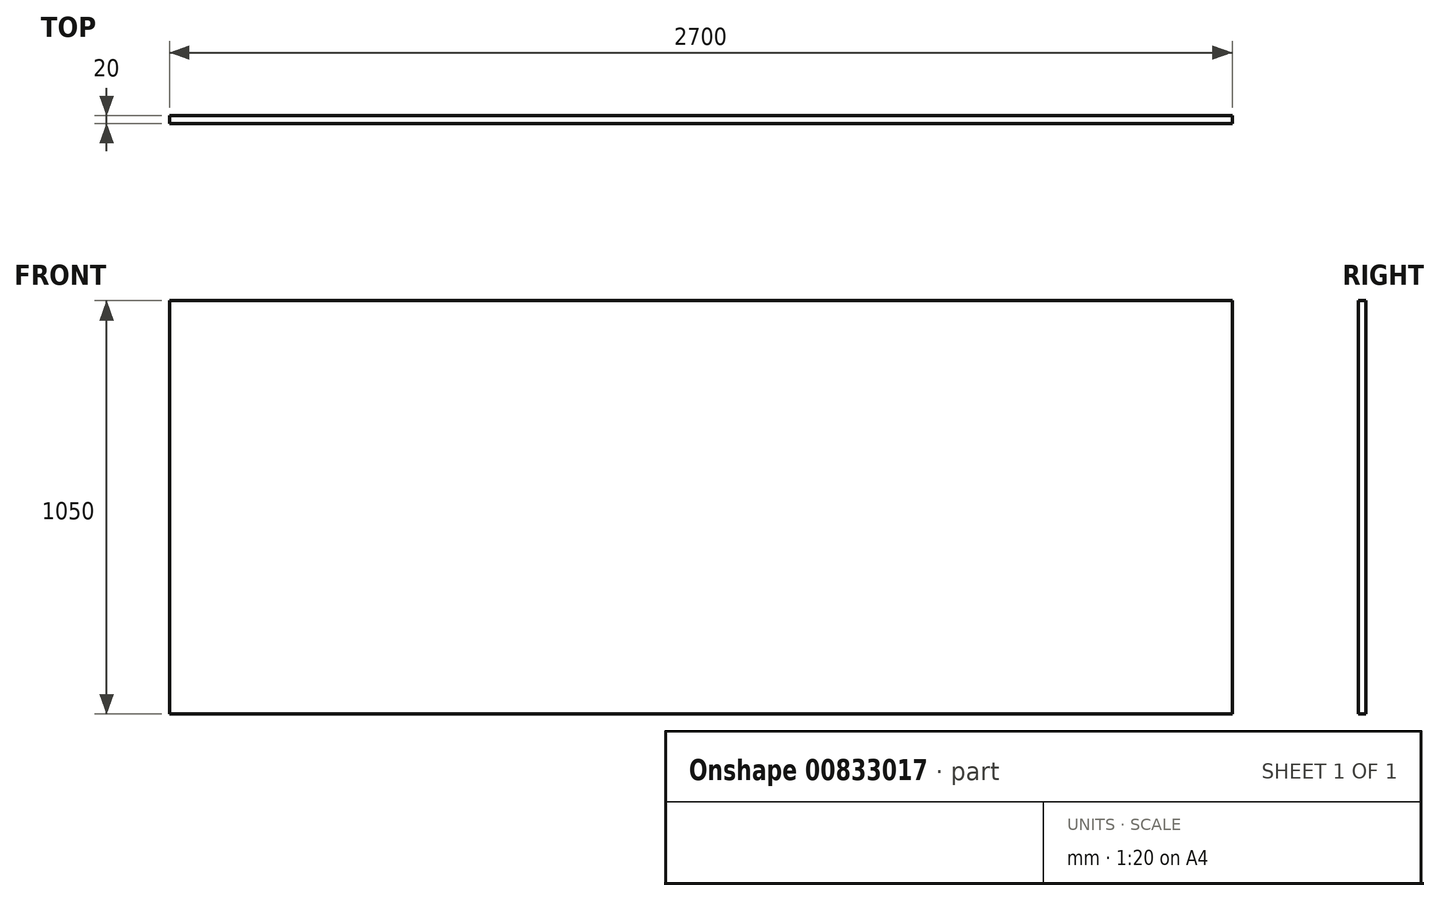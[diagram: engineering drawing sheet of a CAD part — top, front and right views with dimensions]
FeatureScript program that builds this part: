
annotation { "Feature Type Name" : "Feature", "Feature Type Description" : "" }
export const myFeature = defineFeature(function(context is Context, id is Id, definition is map)
    precondition{}
    {
        {
            var Q0;
            Q0=qCreatedBy(makeId("Front.planeOp"),FACE);
            var sketch = newSketch(context, id + "F0", { "sketchPlane" : qUnion([Q0])});
            skLineSegment(sketch, "E0.bottom", {"start": v(-1350, 525) * mm, "end": v(1350, 525) * mm});
            skLineSegment(sketch, "E0.top", {"start": v(-1350, -525) * mm, "end": v(1350, -525) * mm});
            skLineSegment(sketch, "E0.left", {"start": v(-1350, 525) * mm, "end": v(-1350, -525) * mm});
            skLineSegment(sketch, "E0.right", {"start": v(1350, 525) * mm, "end": v(1350, -525) * mm});
            skPoint(sketch, "E0.middle", {"position": v(0, 0) * mm});
            skSolve(sketch);
        }
        {
            var Q0;
            Q0=makeQuery(id+"F0.imprint","IMPRINT",FACE,{"disambiguationData":[TD([[makeQuery(id+"F0.imprint","IMPRINT",EDGE,{"derivedFrom":sQuery(id+"F0.wireOp",EDGE,"E0.bottom")}),-1.0]])]});
            extrude(context, id + "F1", {"entities" : qUnion([Q0]), "depth" : 20 * mm, "offsetDistance" : 25 * mm});
        }
    });
